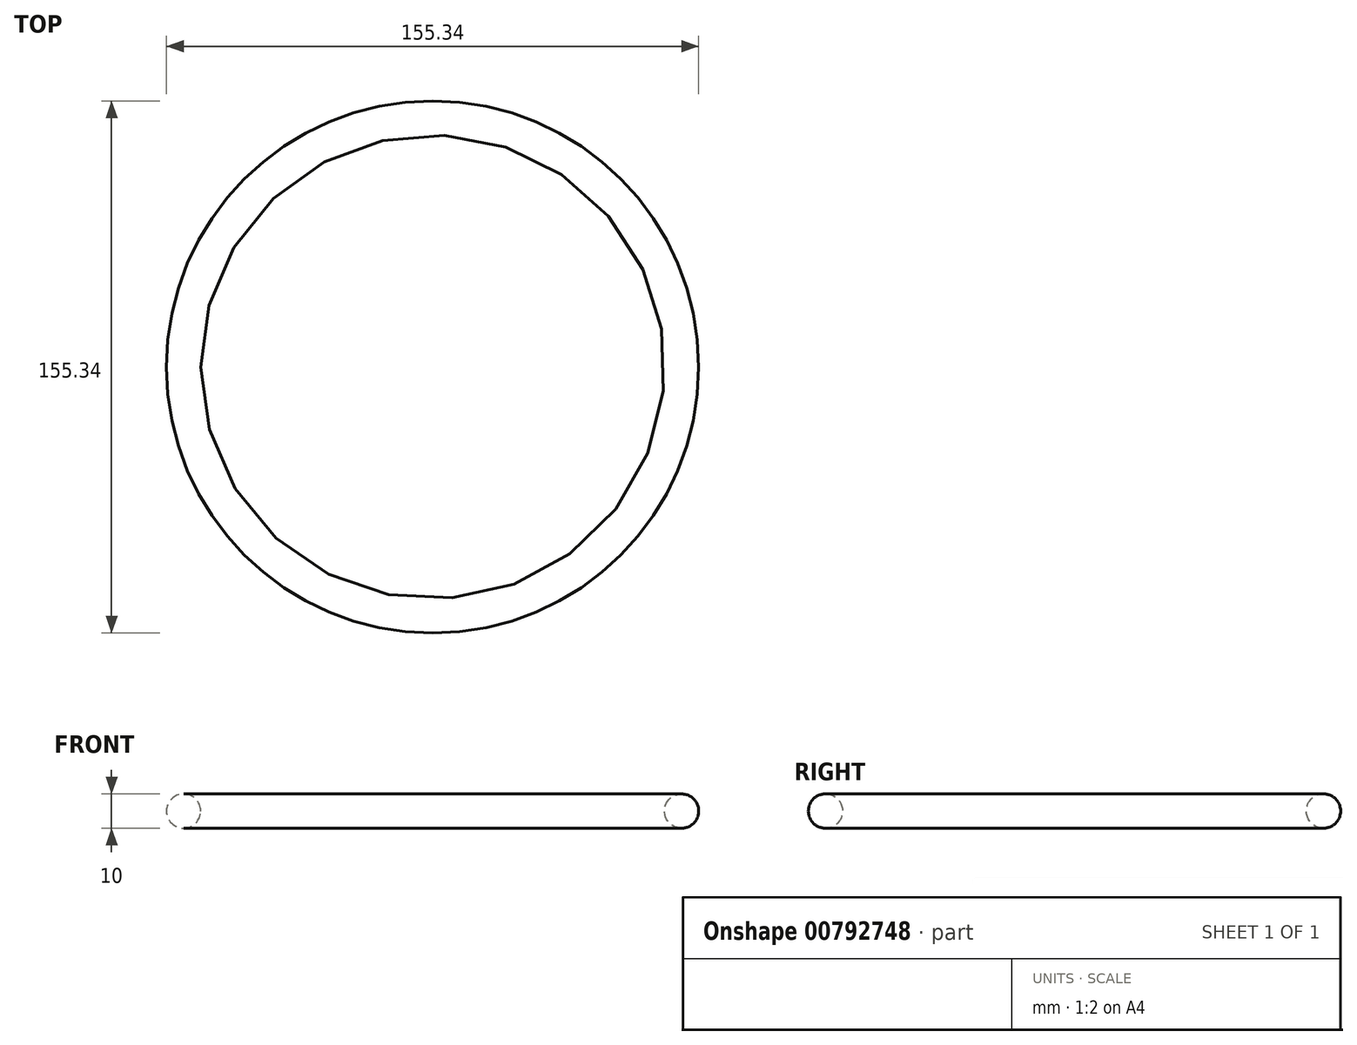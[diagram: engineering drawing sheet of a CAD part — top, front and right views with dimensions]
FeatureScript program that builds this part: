
annotation { "Feature Type Name" : "Feature", "Feature Type Description" : "" }
export const myFeature = defineFeature(function(context is Context, id is Id, definition is map)
    precondition{}
    {
        {
            var Q0;
            Q0=qCreatedBy(makeId("Front.planeOp"),FACE);
            var sketch = newSketch(context, id + "F0", { "sketchPlane" : qUnion([Q0])});
            skCircle(sketch, "E0", {"center": v(0, 1.54) * mm, "radius": 5 * mm});
            skLineSegment(sketch, "E1", {"start": v(-72.67, 4.45) * mm, "end": v(-72.67, 0) * mm});
            skSolve(sketch);
        }
        {
            var Q0;
            Q0=sQuery(id+"F0.wireOp",EDGE,"E0");
            var Q1;
            Q1=sQuery(id+"F0.wireOp",EDGE,"E1");
            revolve(context, id + "F1", {"bodyType" : ToolBodyType.SURFACE, "surfaceOperationType" : NewSurfaceOperationType.NEW, "surfaceEntities" : qUnion([Q0]), "axis" : qUnion([Q1]), "revolveType" : RevolveType.FULL});
        }
    });
